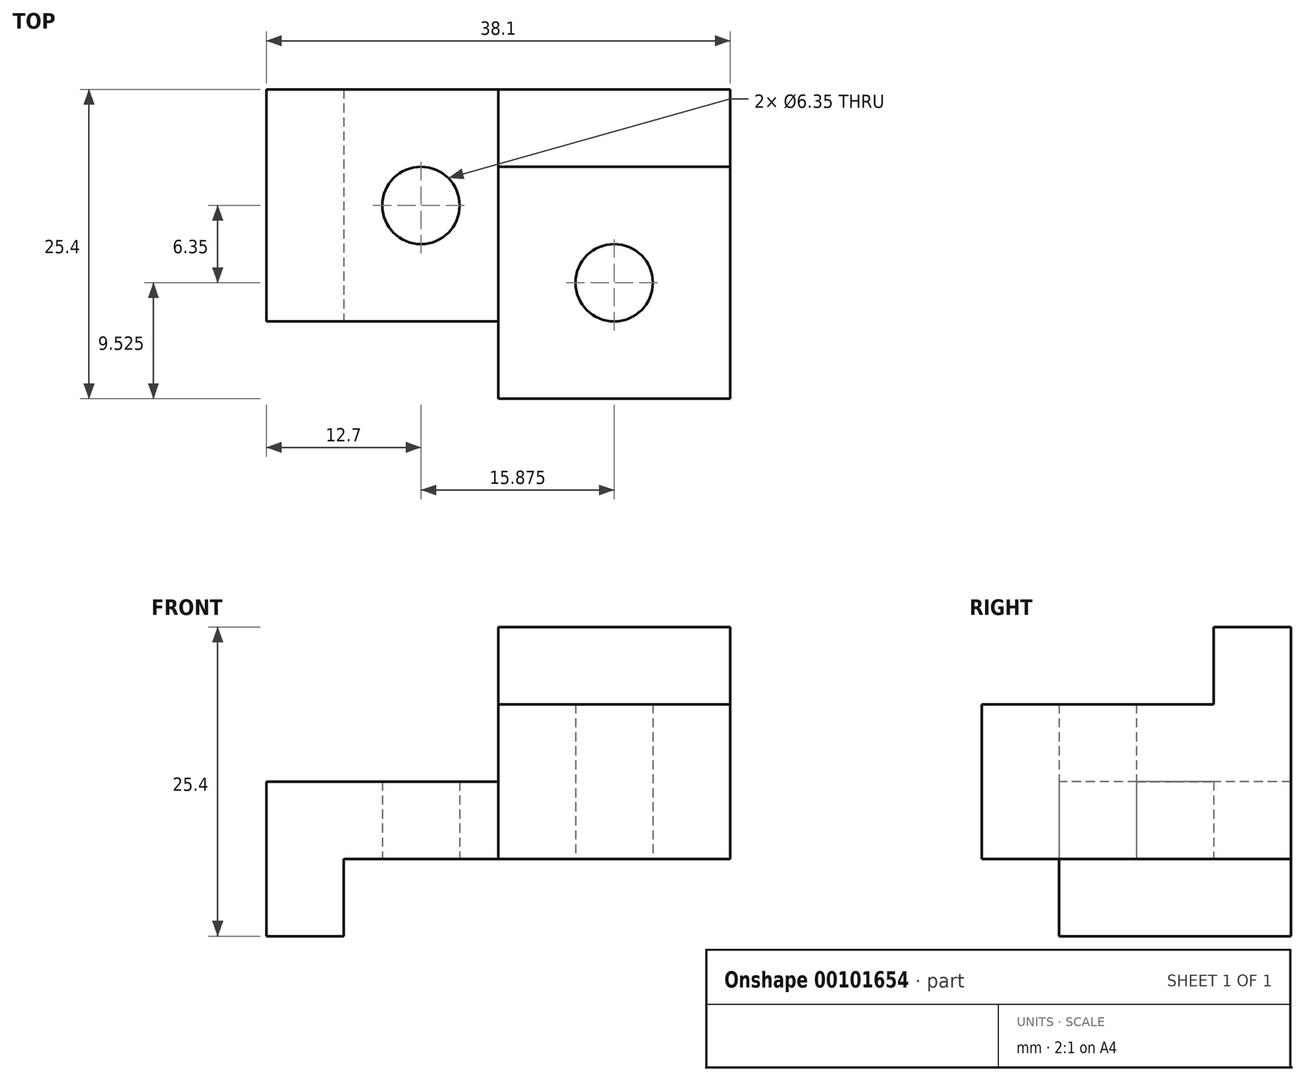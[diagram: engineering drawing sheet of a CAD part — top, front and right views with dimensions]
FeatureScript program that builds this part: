
annotation { "Feature Type Name" : "Feature", "Feature Type Description" : "" }
export const myFeature = defineFeature(function(context is Context, id is Id, definition is map)
    precondition{}
    {
        {
            var Q0;
            Q0=qCreatedBy(makeId("Top.planeOp"),FACE);
            var sketch = newSketch(context, id + "F0", { "sketchPlane" : qUnion([Q0])});
            skLineSegment(sketch, "E0", {"start": v(0, 0) * mm, "end": v(19.05, 0) * mm});
            skLineSegment(sketch, "E1", {"start": v(19.05, 0) * mm, "end": v(19.05, 19.05) * mm});
            skLineSegment(sketch, "E2", {"start": v(19.05, 19.05) * mm, "end": v(0, 19.05) * mm});
            skLineSegment(sketch, "E3", {"start": v(0, 19.05) * mm, "end": v(0, 0) * mm});
            skLineSegment(sketch, "E4", {"start": v(6.35, 19.05) * mm, "end": v(6.35, 0) * mm});
            skLineSegment(sketch, "E5", {"start": v(19.05, 19.05) * mm, "end": v(19.05, -6.35) * mm});
            skLineSegment(sketch, "E6", {"start": v(19.05, -6.35) * mm, "end": v(38.1, -6.35) * mm});
            skLineSegment(sketch, "E7", {"start": v(19.05, 19.05) * mm, "end": v(38.1, 19.05) * mm});
            skLineSegment(sketch, "E8", {"start": v(38.1, 19.05) * mm, "end": v(38.1, -6.35) * mm});
            skLineSegment(sketch, "E9", {"start": v(19.05, 12.7) * mm, "end": v(38.1, 12.7) * mm});
            skCircle(sketch, "E10", {"center": v(12.7, 9.53) * mm, "radius": 3.17 * mm});
            skCircle(sketch, "E11", {"center": v(28.58, 3.17) * mm, "radius": 3.18 * mm});
            skSolve(sketch);
        }
        {
            var Q0;
            Q0 = qSketchRegion(id + "F0", true);
            extrude(context, id + "F1", {"entities" : qUnion([Q0]), "depth" : 6.35 * mm});
        }
        {
            var Q0;
            {var subQ1=sQuery(id+"F0.wireOp",EDGE,"E6");Q0=makeQuery(id+"F0.imprint","IMPRINT",FACE,{"disambiguationData":[TD([[makeQuery(id+"F0.imprint","IMPRINT",EDGE,{"derivedFrom":subQ1}),1.0]])]});}
            extrude(context, id + "F2", {"entities" : qUnion([Q0]), "operationType" : NewBodyOperationType.ADD, "depth" : 12.7 * mm});
        }
        {
            var Q0;
            {var subQ0=sQuery(id+"F0.wireOp",EDGE,"E7");Q0=makeQuery(id+"F0.imprint","IMPRINT",FACE,{"disambiguationData":[TD([[makeQuery(id+"F0.imprint","IMPRINT",EDGE,{"derivedFrom":subQ0}),-1.0]])]});}
            extrude(context, id + "F3", {"entities" : qUnion([Q0]), "operationType" : NewBodyOperationType.ADD, "depth" : 19.05 * mm});
        }
        {
            var Q0;
            {var subQ0=sQuery(id+"F0.wireOp",EDGE,"E3");Q0=makeQuery(id+"F0.imprint","IMPRINT",FACE,{"disambiguationData":[TD([[makeQuery(id+"F0.imprint","IMPRINT",EDGE,{"derivedFrom":subQ0}),1.0]])]});}
            extrude(context, id + "F4", {"entities" : qUnion([Q0]), "operationType" : NewBodyOperationType.ADD, "oppositeDirection" : true, "depth" : 6.35 * mm});
        }
    });
